# Revit family: Specialty_Equipment-Detroit_Radiant-Unit_Heater-ELD_Series-bk1
name_source: partatom
category: Specialty Equipment
units: mm (PartAtom-declared; Revit-internal decimal feet)

## family parameters
Always vertical = No
Cut with Voids When Loaded = No
Enable Cutting in Views = No
Maintain Annotation Orientation = No
OmniClass Number = 23.40.40.14
OmniClass Title = Food Service Equipment
Part Type = Normal
Room Calculation Point = No
Round Connector Dimension = Use Diameter
Shared = No
Work Plane-Based = Yes

## types (4) — shared parameters
Amperage = 0 A
CD_Material_Clearance Zone = Clearance-Detroit_Radiant-Shaded
CD_Material_Finish = Metal-Steel-Detroit_Radiant-Coated_Aluminized_Steel
CD_Prodcut Page URL = https://www.reverberray.com
CD_Product Documentation Link = https://www.reverberray.com
CD_Product Name = ELD-Series heaters
Description = Infrared Electric Heaters
Manufacturer = Detroit Radiant
Power Consumption = 0 VA
URL = https://www.reverberray.com
Voltage = 0 V
zero-valued in all types: Default Elevation

## per-type parameters (varying)
| type | CD_24 | CD_33 | CD_46 | CD_60 | CD_Heater Type | CD_Mounting Width | CD_W Clear | Model |
| ELD - 24" - Single | Yes | No | No | No | Specialty_Equipment-Detroit_Radiant-Unit_Nested_Heater-ELD_Series : ELD - 24" | 23.5 " | 57 " | ELD24 |
| ELD - 33" - Single | No | Yes | No | No | Specialty_Equipment-Detroit_Radiant-Unit_Nested_Heater-ELD_Series : ELD - 33" | 32.5 " | 66 " | ELD33 |
| ELD - 46" - Single | No | No | Yes | No | Specialty_Equipment-Detroit_Radiant-Unit_Nested_Heater-ELD_Series : ELD - 46" | 45.5 " | 79 " | ELD46 |
| ELD - 60" - Single | No | No | No | Yes | Specialty_Equipment-Detroit_Radiant-Unit_Nested_Heater-ELD_Series : ELD - 60" | 59.5 " | 93 " | ELD60 |

## geometry (parser evidence)
native form markers: Sweep x7
no freeform markers — native parametric forms only
